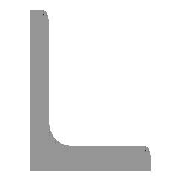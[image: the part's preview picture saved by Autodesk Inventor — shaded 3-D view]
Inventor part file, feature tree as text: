
AUTODESK INVENTOR PART (.ipt)
format: ipt  version: 2013 (Build 170138000, 138)  size: 129,024 bytes
history: native  units: mm (DEFAULTED — no unit token found)
features: other x4, plane x3, split x2, sketch x2
ambient origin geometry x8: Origin, YZ Plane, XZ Plane, XY Plane, X Axis, Y Axis, Z Axis, Center Point
bodies: Solid1 (feature_tree), Body (feature_tree)
feature tree (11):
  parser-record x1  (decoder bookkeeping rows leaked as tree rows — omitted from the tree; the rows remain in map.json)
  other  "Driven Length"
  other  "Start plane"
  other  "End plane"
  plane  "Work Plane4"
  split  "Split1"
  plane  "Work Plane5"
  split  "Split2"
  sketch  "Sketch3"  dims[d0=38.1mm]
  plane  "Work Plane3"
  sketch  "Sketch4"  dims[d1=38.1mm d2=4.7625mm d3=4.7625mm d4=1066.8mm d5=0.0mm d10=0.0mm d11=0.0mm d12=-0.0mm d13=1066.8mm d14=4.826mm d15=2.286mm d16=90.0deg d17=1066.8mm]
